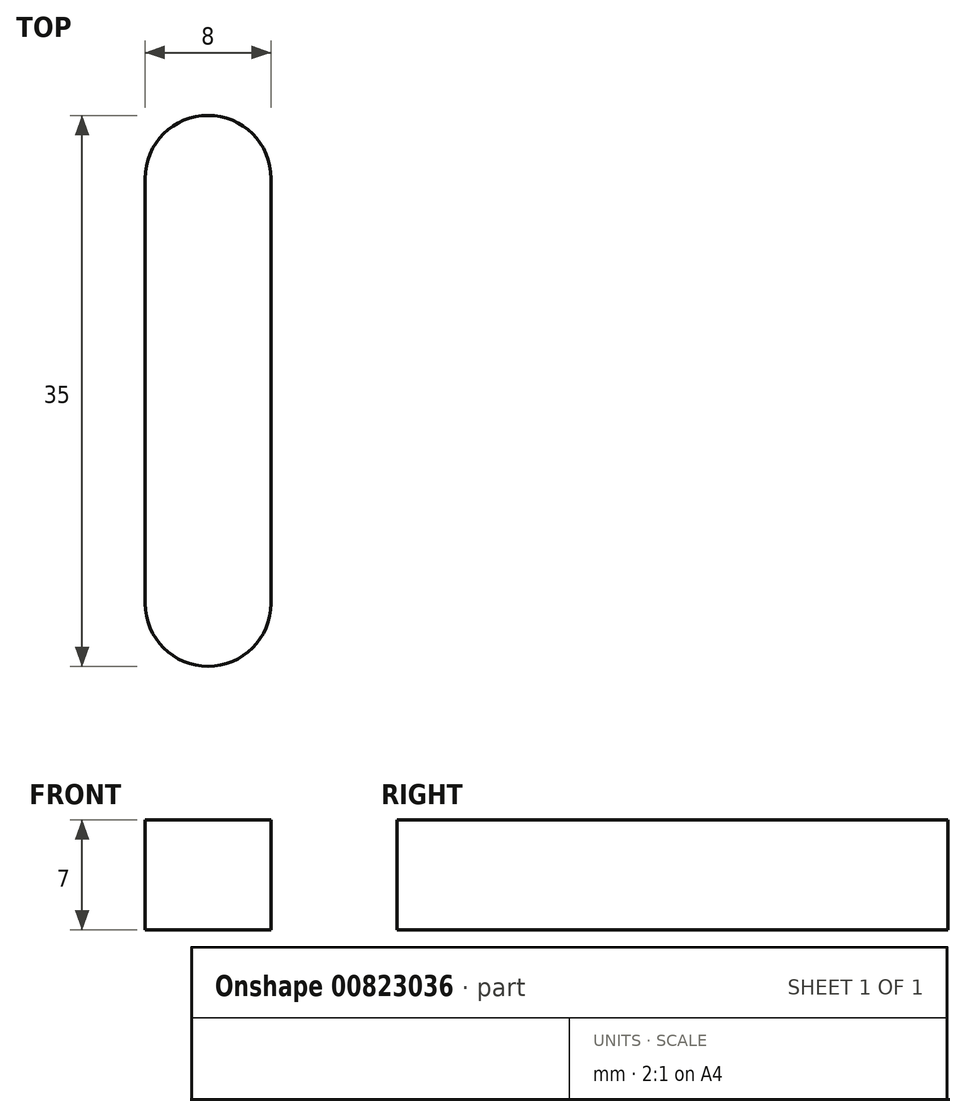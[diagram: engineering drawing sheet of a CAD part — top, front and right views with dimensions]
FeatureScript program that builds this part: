
annotation { "Feature Type Name" : "Feature", "Feature Type Description" : "" }
export const myFeature = defineFeature(function(context is Context, id is Id, definition is map)
    precondition{}
    {
        {
            var Q0;
            Q0=qCreatedBy(makeId("Top.planeOp"),FACE);
            var sketch = newSketch(context, id + "F0", { "sketchPlane" : qUnion([Q0])});
            skLineSegment(sketch, "E0.left", {"start": v(4, 13.5) * mm, "end": v(4, -13.5) * mm});
            skLineSegment(sketch, "E0.right", {"start": v(-4, 13.5) * mm, "end": v(-4, -13.5) * mm});
            skPoint(sketch, "E0.middle", {"position": v(0, 0) * mm});
            skArc(sketch, "E1", {"start": v(4, 13.5) * mm, "mid": v(0, 17.5) * mm, "end": v(-4, 13.5) * mm});
            skArc(sketch, "E2", {"start": v(-4, -13.5) * mm, "mid": v(0, -17.5) * mm, "end": v(4, -13.5) * mm});
            skSolve(sketch);
        }
        {
            var Q0;
            Q0=qSketchRegion(id+"F0",true);
            extrude(context, id + "F1", {"entities" : qUnion([Q0]), "depth" : 7 * mm, "offsetDistance" : 25 * mm});
        }
    });
